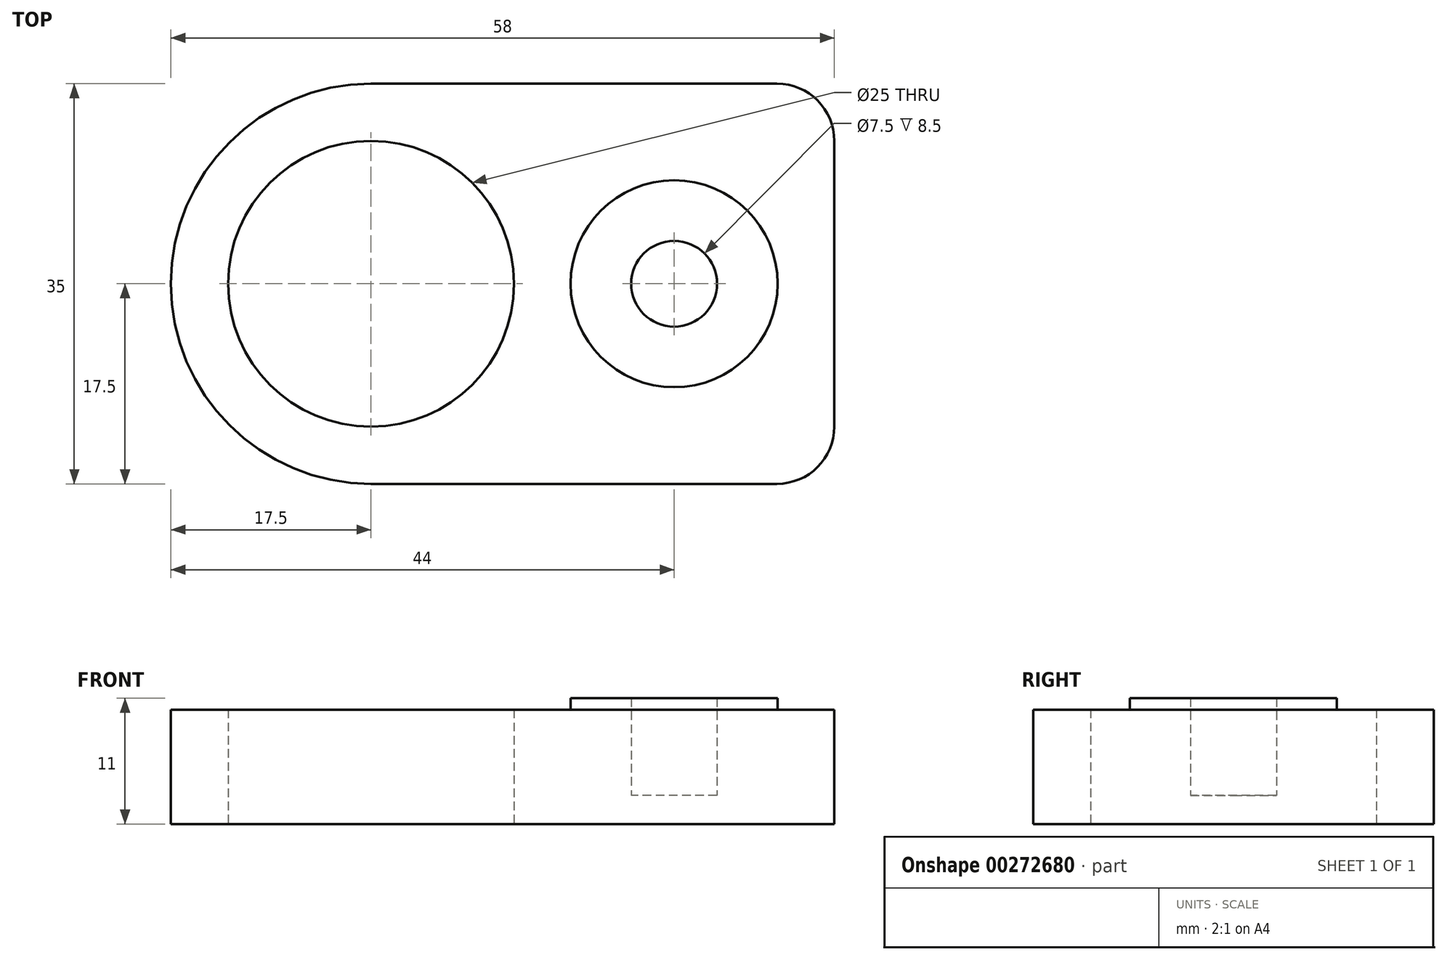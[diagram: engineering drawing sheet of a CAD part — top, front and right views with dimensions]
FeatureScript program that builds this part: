
annotation { "Feature Type Name" : "Feature", "Feature Type Description" : "" }
export const myFeature = defineFeature(function(context is Context, id is Id, definition is map)
    precondition{}
    {
        {
            var Q0;
            Q0=qCreatedBy(makeId("Top.planeOp"),FACE);
            var sketch = newSketch(context, id + "F0", { "sketchPlane" : qUnion([Q0])});
            skLineSegment(sketch, "E0.bottom", {"start": v(17.5, 0) * mm, "end": v(53, 0) * mm});
            skLineSegment(sketch, "E0.top", {"start": v(17.5, 35) * mm, "end": v(53, 35) * mm});
            skLineSegment(sketch, "E0.left", {"start": v(0, 17.5) * mm, "end": v(0, 17.5) * mm});
            skLineSegment(sketch, "E0.right", {"start": v(58, 5) * mm, "end": v(58, 30) * mm});
            skLineSegment(sketch, "E1.bottom", {"start": v(0, 0) * mm, "end": v(17.5, 0) * mm, "construction": true});
            skLineSegment(sketch, "E1.top", {"start": v(0, 17.5) * mm, "end": v(17.5, 17.5) * mm, "construction": true});
            skLineSegment(sketch, "E1.left", {"start": v(0, 0) * mm, "end": v(0, 17.5) * mm, "construction": true});
            skLineSegment(sketch, "E1.right", {"start": v(17.5, 0) * mm, "end": v(17.5, 17.5) * mm, "construction": true});
            skCircle(sketch, "E2", {"center": v(17.5, 17.5) * mm, "radius": 12.5 * mm});
            skPoint(sketch, "E3.visualSharp", {"position": v(0, 0) * mm});
            skArc(sketch, "E3.filletArc", {"start": v(0, 17.5) * mm, "mid": v(5.13, 5.13) * mm, "end": v(17.5, 0) * mm});
            skPoint(sketch, "E4.visualSharp", {"position": v(0, 35) * mm});
            skArc(sketch, "E4.filletArc", {"start": v(17.5, 35) * mm, "mid": v(5.13, 29.87) * mm, "end": v(0, 17.5) * mm});
            skPoint(sketch, "E5.visualSharp", {"position": v(58, 35) * mm});
            skArc(sketch, "E5.filletArc", {"start": v(58, 30) * mm, "mid": v(56.54, 33.54) * mm, "end": v(53, 35) * mm});
            skPoint(sketch, "E6.visualSharp", {"position": v(58, 0) * mm});
            skArc(sketch, "E6.filletArc", {"start": v(53, 0) * mm, "mid": v(56.54, 1.46) * mm, "end": v(58, 5) * mm});
            skSolve(sketch);
        }
        {
            var Q0;
            Q0=makeQuery(id+"F0.imprint","IMPRINT",FACE,{"disambiguationData":[TD([[makeQuery(id+"F0.imprint","IMPRINT",EDGE,{"derivedFrom":sQuery(id+"F0.wireOp",EDGE,"E0.bottom")}),1.0]])]});
            extrude(context, id + "F1", {"entities" : qUnion([Q0]), "depth" : 10 * mm});
        }
        {
            var Q0;
            Q0=makeQuery(id+"F1.opExtrude","CAP_FACE",FACE,{"disambiguationData":[OSD([sQuery(id+"F0.wireOp",EDGE,"E0.bottom"),sQuery(id+"F0.wireOp",EDGE,"E0.top"),sQuery(id+"F0.wireOp",EDGE,"E0.right"),sQuery(id+"F0.wireOp",EDGE,"E2"),sQuery(id+"F0.wireOp",EDGE,"E3.filletArc"),sQuery(id+"F0.wireOp",EDGE,"E4.filletArc"),sQuery(id+"F0.wireOp",EDGE,"E5.filletArc"),sQuery(id+"F0.wireOp",EDGE,"E6.filletArc")])],"isStart":false});
            var sketch = newSketch(context, id + "F2", { "sketchPlane" : qUnion([Q0])});
            skLineSegment(sketch, "E7.bottom", {"start": v(0, 0) * mm, "end": v(44, 0) * mm, "construction": true});
            skLineSegment(sketch, "E7.top", {"start": v(0, 17.5) * mm, "end": v(44, 17.5) * mm, "construction": true});
            skLineSegment(sketch, "E7.left", {"start": v(0, 0) * mm, "end": v(0, 17.5) * mm, "construction": true});
            skLineSegment(sketch, "E7.right", {"start": v(44, 0) * mm, "end": v(44, 17.5) * mm, "construction": true});
            skCircle(sketch, "E8", {"center": v(44, 17.5) * mm, "radius": 9.05 * mm});
            skCircle(sketch, "E9", {"center": v(44, 17.5) * mm, "radius": 3.75 * mm});
            skSolve(sketch);
        }
        {
            var Q0;
            Q0=makeQuery(id+"F2.imprint","IMPRINT",FACE,{"disambiguationData":[TD([[makeQuery(id+"F2.imprint","IMPRINT",EDGE,{"derivedFrom":sQuery(id+"F2.wireOp",EDGE,"E8")}),1.0]])]});
            extrude(context, id + "F3", {"entities" : qUnion([Q0]), "operationType" : NewBodyOperationType.ADD, "depth" : 1 * mm});
        }
        {
            var Q0;
            Q0=makeQuery(id+"F2.imprint","IMPRINT",FACE,{"disambiguationData":[TD([[makeQuery(id+"F2.imprint","IMPRINT",EDGE,{"derivedFrom":sQuery(id+"F2.wireOp",EDGE,"E9")}),1.0]])]});
            extrude(context, id + "F4", {"entities" : qUnion([Q0]), "operationType" : NewBodyOperationType.REMOVE, "oppositeDirection" : true, "depth" : 7.5 * mm});
        }
    });
